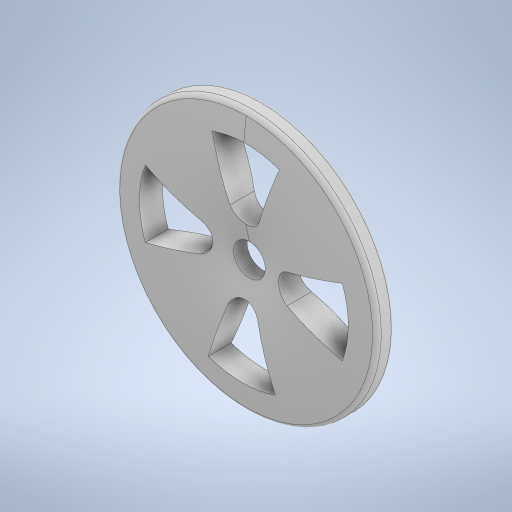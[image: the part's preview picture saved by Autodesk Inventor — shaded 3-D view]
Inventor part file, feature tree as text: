
AUTODESK INVENTOR PART (.ipt)
format: ipt  version: 2023 (Build 270158000, 158)  size: 427,008 bytes
history: native  units: in
note: dims shown in document units (in); Inventor stores cm internally (conversion verified against a paired STEP export)
features: sketch x3, extrude x2, revolve x1
ambient origin geometry x8: Origin, YZ Plane, XZ Plane, XY Plane, X Axis, Y Axis, Z Axis, Center Point
bodies: Solid1 (feature_tree)
feature tree (6):
  revolve  "Revolution1"  [1 undecoded]
  extrude  "Extrusion1"  Depth=4.1437in TaperAngle=0.0deg
  extrude  "Extrusion3"  Depth=4.1437in TaperAngle=0.0deg
  sketch  "Sketch1"  dims[d0=0.0787in d1=0.0787in]
  sketch  "Sketch2"  dims[d2=90.0deg d3=4.1437in d4=0.0in]
  sketch  "Sketch3"  dims[d11=1.5748in d13=360.0deg d15=4.1437in d16=0.0in d9=0.0197in d10=0.0344in d12=0.0344in]
note: 1 required parameter value undecoded (feature->parameter linkage not recoverable at this tier; creation-order binding heuristic only, values carry confidence <= 0.55)
